# Revit family: Sanitary_Waste-Bins_Dandent_AFB-210_Big
name_source: partatom
category: Furniture
revit_build: Autodesk Revit 2017 (Build: 20190508_0315(x64)
units: mm (PartAtom-declared; Revit-internal decimal feet)

## family parameters
Always vertical = Yes
Cut with Voids When Loaded = No
OmniClass Number = 23.40.20.31
OmniClass Title = Refuse Disposal Furniture
Room Calculation Point = No
Shared = No
Work Plane-Based = No

## types (1)
- Large waste bin - AFB210
    AssetType = Movable
    BIMObjectName = Sanitary_Waste-Bins_Dandent_AFB-210_Big
    Brand = Dandent
    Category = Waste bin
    Color = Grey
    ConvergoRefNr = 0151-1909-0002-SE
    Cost = 0 $
    DurationUnit = Year
    Features = 120 liter capacity, wheels
    Finish = Grey lacquered steel
    IfcExportAs = IfcFurnitureType
    IfcExportType = BIN
    MainColor = Grey
    Manufacturer = Dandent
    ManufacturerName = Dandent
    ManufacturerURL = https://www.dandent.se
    Material = Steel, plastic
    Model = Large waste bin - AFB210
    ModelNumber = AFB210
    NBSDescription = Waste bins
    NBSReference = 45-35-72/380
    Name = Dandent_AFB-210_Big
    NominalDepth = 450 mm  [stored 1.47638 ft]
    NominalHeight = 770 mm  [stored 2.52625 ft]
    NominalLength = 490 mm  [stored 1.60761 ft]
    Product data url = https://www.bimobject.com
    Shape = Rectangular
    Size = 490x450x770 mm
    URL = https://www.dandent.se
    Uniclass2 = Pr_40_50_07_76
    Uniclass2015Description = Waste bins
    Uniclass2015Reference = Pr_40_50_07_96
    Version = 1
    VersionDate = 12/09/2019
    WarrantyDurationUnit = Year
    WastebinMainMaterial = Grey lacquered steel
    WastebinSecondaryMaterial = Plastic, Opaque White

note: [stored X ft] marks values corroborated as IEEE doubles in the binary element streams (Revit-internal decimal feet)

## geometry (parser evidence)
native form markers: Sweep x5
no freeform markers — native parametric forms only
